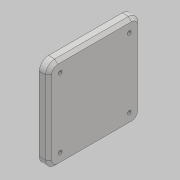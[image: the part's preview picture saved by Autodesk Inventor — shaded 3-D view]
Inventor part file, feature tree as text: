
AUTODESK INVENTOR PART (.ipt)
format: ipt  version: 2018 (Build 220112000, 112)  size: 126,464 bytes
history: native  units: mm
features: sketch x3, hole x3, other x1, extrude x1, fillet x1, chamfer x1, projected_geometry x1
ambient origin geometry x8: Origin, YZ Plane, XZ Plane, XY Plane, X Axis, Y Axis, Z Axis, Center Point
bodies: Body1 (feature_tree)
feature tree (11):
  other  "實體1"
  extrude  "擠出1"  Depth=300.0mm
  fillet  "圓角1"  Radius=300.0mm
  chamfer  "倒角1"  Distance=30.0mm
  sketch  "草圖2"
  hole  "孔1"  [1 undecoded]
  hole  "孔2"  [1 undecoded]
  hole  "孔3"  [1 undecoded]
  sketch  "草圖1"
  sketch  "草圖3"
  projected_geometry  "投影迴路1"
note: 3 required parameter values undecoded (feature->parameter linkage not recoverable at this tier; creation-order binding heuristic only, values carry confidence <= 0.55)
